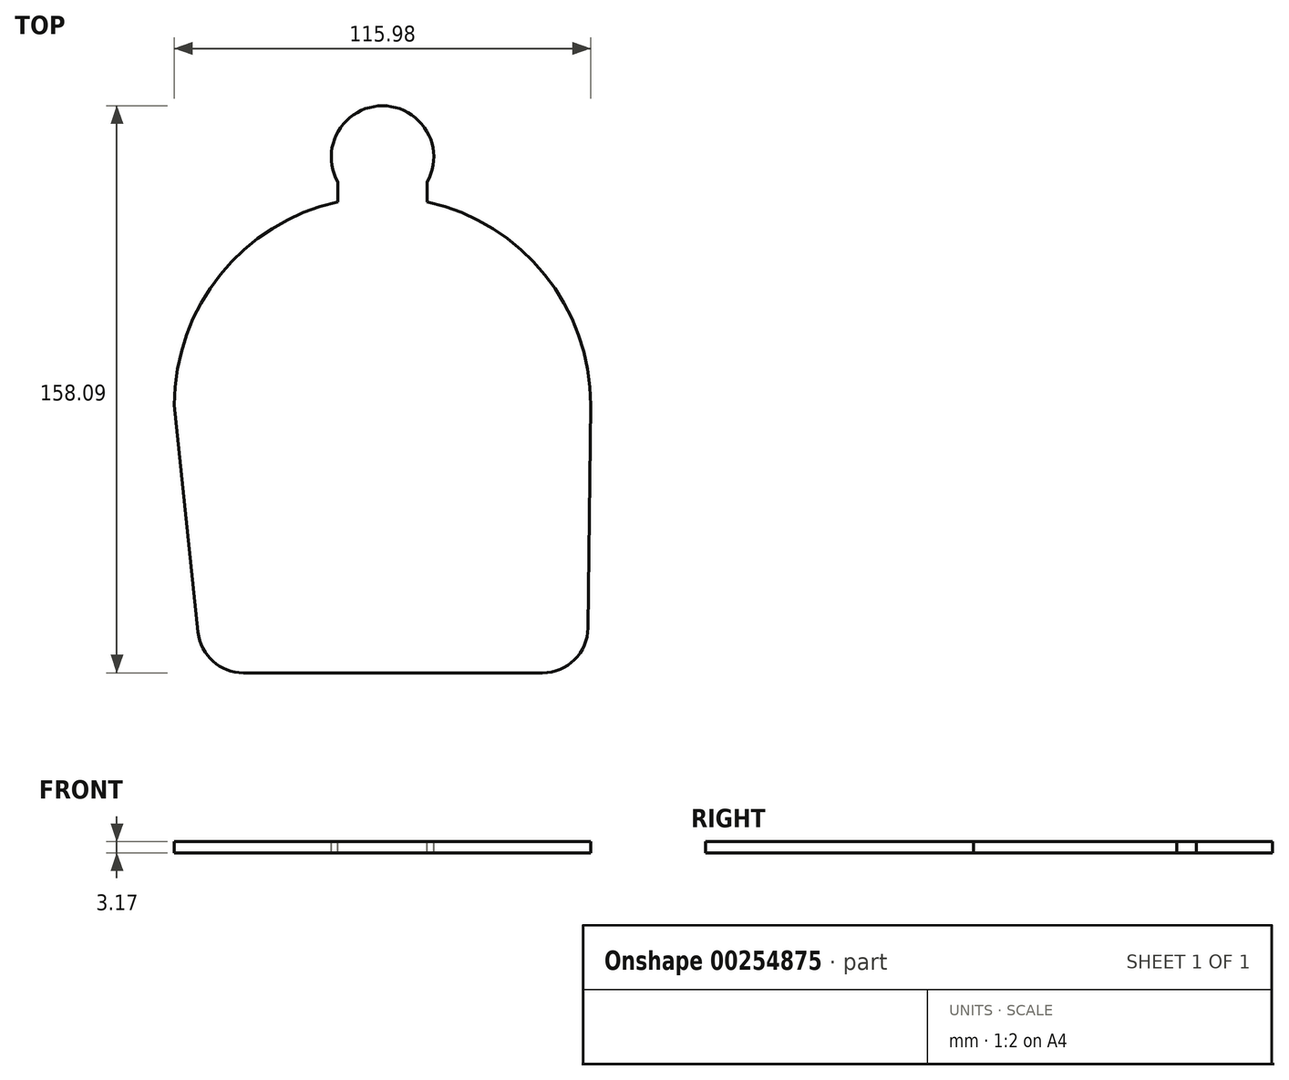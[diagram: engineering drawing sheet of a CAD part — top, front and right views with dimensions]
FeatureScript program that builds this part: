
annotation { "Feature Type Name" : "Feature", "Feature Type Description" : "" }
export const myFeature = defineFeature(function(context is Context, id is Id, definition is map)
    precondition{}
    {
        {
            var Q0;
            Q0=qCreatedBy(makeId("Top.planeOp"),FACE);
            var sketch = newSketch(context, id + "F0", { "sketchPlane" : qUnion([Q0])});
            skLineSegment(sketch, "E0.0", {"start": v(-38.75, -74.7) * mm, "end": v(44.57, -74.7) * mm});
            skArc(sketch, "E1", {"start": v(57.99, 0) * mm, "mid": v(45.2, 36.32) * mm, "end": v(12.48, 56.63) * mm});
            skLineSegment(sketch, "E2", {"start": v(-57.99, 0) * mm, "end": v(-51.38, -63.32) * mm});
            skLineSegment(sketch, "E3", {"start": v(57.99, 0) * mm, "end": v(57.27, -62.15) * mm});
            skArc(sketch, "E4.filletArc", {"start": v(-51.38, -63.32) * mm, "mid": v(-47.25, -71.44) * mm, "end": v(-38.75, -74.7) * mm});
            skArc(sketch, "E5.filletArc", {"start": v(44.57, -74.7) * mm, "mid": v(53.5, -71.04) * mm, "end": v(57.27, -62.15) * mm});
            skArc(sketch, "E6.trimOffspring", {"start": v(-12.48, 56.63) * mm, "mid": v(-45.2, 36.32) * mm, "end": v(-57.99, 0) * mm});
            skLineSegment(sketch, "E7.0", {"start": v(12.48, 56.63) * mm, "end": v(12.48, 62.14) * mm});
            skLineSegment(sketch, "E8.0", {"start": v(-12.48, 56.63) * mm, "end": v(-12.48, 62.14) * mm});
            skArc(sketch, "E9.0", {"start": v(12.48, 62.14) * mm, "mid": v(0, 83.39) * mm, "end": v(-12.48, 62.14) * mm});
            skSolve(sketch);
        }
        {
            var Q0;
            Q0=makeQuery(id+"F0.imprint","IMPRINT",FACE,{"disambiguationData":[TD([[makeQuery(id+"F0.imprint","IMPRINT",EDGE,{"derivedFrom":sQuery(id+"F0.wireOp",EDGE,"E0.0")}),1.0]])]});
            extrude(context, id + "F1", {"entities" : qUnion([Q0]), "oppositeDirection" : true, "depth" : 3.17 * mm});
        }
    });
